# Revit family: Artemide_Discovery_Floor
name_source: partatom
category: Lighting Fixtures
revit_build: Autodesk Revit 2018 (Build: 20170223_1515(x64)
units: mm (PartAtom-declared; Revit-internal decimal feet)

## family parameters
Always vertical = No
Cut with Voids When Loaded = No
Light Source = Yes
Part Type = Normal
Room Calculation Point = No
Round Connector Dimension = Use Diameter
Shared = No
Work Plane-Based = Yes

## types (3) — shared parameters
6 Monthly = -
Air Handling = -
Annually = -
Application Environment = Internal
Beam Angle Longditudinal Axis  = 0.00°
Beam Angle Transverse Axis  = 0.00°
Bespoke Timeframe = -
CE Approval = YES
Cable Material = -
Color Filter = 16777215
Column = -
Control Gear Location = -
Control Gear Required = -
Control Gear Type = -
Daily = -
Daylight Sensor = -
Default Elevation = 1219 mm
Diffuser Finish = -
Diffuser Material  = Technopolymer
Diffusing screen = -
Dimming Lamp Color Temperature Shift = <None>
ENEC Certification of European conformity = Y
Earth Point  = -
Emergency = N
Emergency Lighting Battery = -
Emit Shape Visible in Rendering = No
Emit from Rectangle Length = 360 mm  [stored 1.1811 ft]
Emit from Rectangle Width = 1530 mm  [stored 5.01969 ft]
End Caps/Transition Caps/Joints = -
Environmental Product Declaration = -
Expected Life = -
Face Shape = Rectangular
Features = -
Fire Rated = -
Fire Shroud = -
Fixing Material = -
Fixings = -
Gasket Material = -
Green Guide for Specification = -
Hazardous Area Category = -
Hazardous Area Protection Type = -
Housing Colour  = Black
Housing Finish  = Painted
Housing Material = Aluminum
IES Files  = https://www.artemide.com
IK Rating = -
IfcExportAs = IfcLightFixtureType
IfcExportType = NOT DEFINED
Infills = -
Integral Emergency Lighting Battery Type = -
Integral Fuse or Circuit Protection  = -
Intended Market = Unset
International Type Code = -
Lamp Cap = LED Integrated
Lamp Holder Material = -
Lamp Included = Y
Lamp Replacement Interval = -
Lamp Survival Factor = -
Life Cycle Analysis = -
Light Fixture Mounting Type = Leaning
Light Output Pattern = -
Location of Manufacturer = -
Louvre/Lens = -
Luminaire Cleaning Interval  = -
Luminaire Type = Floor
M_Housing = Artemide_Aluminum_Black
Maintenance Required: 0-300hrs  = -
Maintenance Required: 1001-2000hrs  = -
Maintenance Required: 2001-4000hrs  = -
Maintenance Required: 301-600hrs  = -
Maintenance Required: 4001-8000hrs  = -
Maintenance Required: 601-1000hrs = -
Maintenance Required: 8001-12000hrs  = -
Manufacturer = Artemide
Manufacturer Website = https://www.artemide.com
Material Ingredient Reporting = -
Monthly = -
Motion Detector = -
Motion Sensor = -
Number of Primary Lamps = 1
Overall Height = 1.7e-05
Overall Length = 1570
Overall Width = 400
Photocell = -
Photometric Web File = 2041030APP.IES
Power Supply Kit = -
Primary Lamp Type = LED
Product Literature = Artemide - Discovery Floor
Product Range = Discovery Floor
Quarterly = -
Reflector Finish = -
Reflector Material = -
Responsible Extraction of Materials = -
Responsible Sourcing of Materials = -
Secondary Lamp = N
Secondary Lamp Cap = -
Secondary Lamp Included = -
Secondary Lamp International Type Code = -
Service life  = -
Standards = -
Suitable Dimmer Type = APP
Suitable for Dimming  = Y
Suitable for Motion Detector Control = N
Suitable for Photocell Control = -
Testing method = -
Tilt Angle = 90.00°
Trim Colour  = -
Trim Finish = -
Trim Material = -
URL to Energy Technology List = -
URL to O&M Manual = https://www.artemide.com
Uniclass 2015 = Pr_70_70_48
Unified Glare Rating  = -
Voltage = -
Warranty ID = https://cloud.artemide.com
Weekly = -
zero-valued in all types: Access Clearance Bottom, Access Clearance Front, Access Clearance Left, Access Clearance Rear, Access Clearance Right, Access Clearance Top, Ambient Temperature                            , Basis of lifetime lumen depreciation  , Basis of lifetime luminaire failures       , Control Gear Standby Power , Current , Cut Out Length, Cut Out Width, Downward Component, Drive Current                                         , Duration of Integral Emergency Lighting , Efficacy_2, Efficiency, Embodied Carbon , Emergency Charging Power      , Emergency light output percentage, External Control Line Voltage, Face Length, Face Width, Fire Rated Temperature, Fire Rating Duration, Frequency , Gross Weight, Input Lumens Direct light, Input Lumens Indirect light, LED Initial Colour Variation                     , LED Maintained Colour Variation        , Luminaire Maintenance Factor, Luminance at 65deg Angle, Max Height from ceiling, Maximum Operating Temperature, Minimum Operating Temperature, Number of Poles, Number of Secondary Lamps, Output Lumens Direct light, Output Lumens Indirect light, Overall Light Output Ratio, Power Factor, Rated Lamp Life, Secondary Lamp Colour Rendering Index, Secondary Lamp Colour Temperature, Secondary Lamp Efficacy, Secondary Lamp Initial Lumens , Secondary Lamp Voltage, Secondary Rated Lamp Life, Shipping Weight, Supply Phase, Total Light Output , Total Power, Upward Component 

## per-type parameters (varying)
| type | Colour Rendering Index | Colour Temperature | IP Rating | Initial Lumens | LED lifetime | M_Diffuser | Product Model Number |
| Discovery_Floor_Black_White Violet Integralis_2040030IN1APP | 0 | 2700 | - | 2972 | 0 | Artemide_Glass_LightBulbRGB_Violet | 2040030IN1APP |
| Discovery_Floor_Black_RGBW_2041030APP | 80 | 0 | IP20 | 1036 | 50000 | Artemide_Glass_LightBulbRGB | 2041030APP |
| Discovery_Floor_Black_TW_2040030APP | 80 | 0 | IP20 | 2400 | 0 | Artemide_Glass_LightBulb | 2040030APP |

note: [stored X ft] marks values corroborated as IEEE doubles in the binary element streams (Revit-internal decimal feet)

## geometry (parser evidence)
native form markers: Blend x2, Sweep x6
no freeform markers — native parametric forms only
